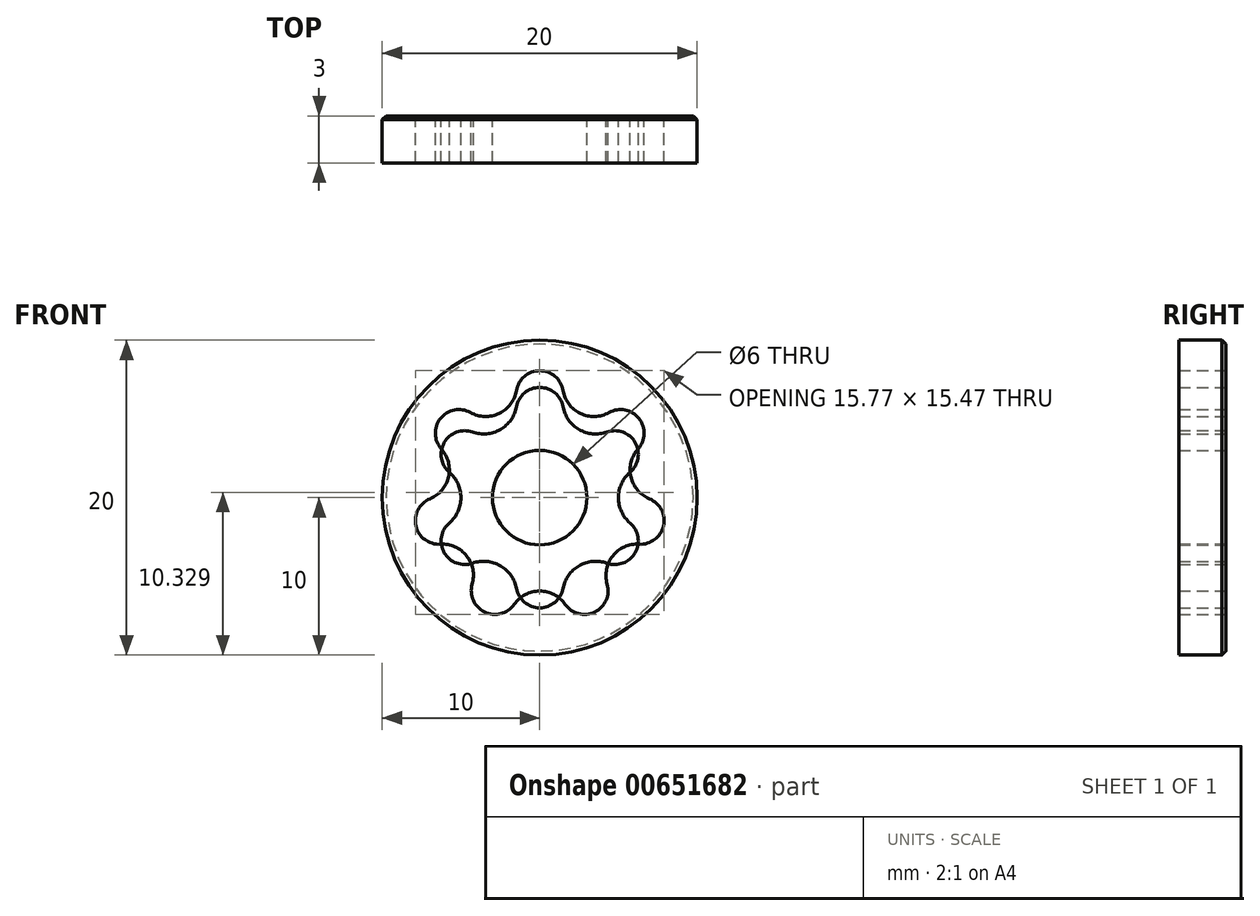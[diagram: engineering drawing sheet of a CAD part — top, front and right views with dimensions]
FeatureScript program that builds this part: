
annotation { "Feature Type Name" : "Feature", "Feature Type Description" : "" }
export const myFeature = defineFeature(function(context is Context, id is Id, definition is map)
    precondition{}
    {
        {
            var Q0;
            Q0=qCreatedBy(makeId("Front.planeOp"),FACE);
            var sketch = newSketch(context, id + "F0", { "sketchPlane" : qUnion([Q0])});
            skArc(sketch, "E0", {"start": v(1.47, 5.78) * mm, "mid": v(0, 7) * mm, "end": v(-1.47, 5.78) * mm});
            skArc(sketch, "E1", {"start": v(1.47, 5.78) * mm, "mid": v(2.5, 4.33) * mm, "end": v(4.27, 4.17) * mm});
            skArc(sketch, "E2.1.0", {"start": v(-4.27, 4.17) * mm, "mid": v(-6.06, 3.5) * mm, "end": v(-5.74, 1.61) * mm});
            skArc(sketch, "E2.1.1", {"start": v(-4.27, 4.17) * mm, "mid": v(-2.5, 4.33) * mm, "end": v(-1.47, 5.78) * mm});
            skArc(sketch, "E2.2.0", {"start": v(-5.74, -1.61) * mm, "mid": v(-6.06, -3.5) * mm, "end": v(-4.27, -4.17) * mm});
            skArc(sketch, "E2.2.1", {"start": v(-5.74, -1.61) * mm, "mid": v(-5, 0) * mm, "end": v(-5.74, 1.61) * mm});
            skArc(sketch, "E2.3.0", {"start": v(-1.47, -5.78) * mm, "mid": v(0, -7) * mm, "end": v(1.47, -5.78) * mm});
            skArc(sketch, "E2.3.1", {"start": v(-1.47, -5.78) * mm, "mid": v(-2.5, -4.33) * mm, "end": v(-4.27, -4.17) * mm});
            skArc(sketch, "E2.4.0", {"start": v(4.27, -4.17) * mm, "mid": v(6.06, -3.5) * mm, "end": v(5.74, -1.61) * mm});
            skArc(sketch, "E2.4.1", {"start": v(4.27, -4.17) * mm, "mid": v(2.5, -4.33) * mm, "end": v(1.47, -5.78) * mm});
            skArc(sketch, "E2.5.0", {"start": v(5.74, 1.61) * mm, "mid": v(6.06, 3.5) * mm, "end": v(4.27, 4.17) * mm});
            skArc(sketch, "E2.5.1", {"start": v(5.74, 1.61) * mm, "mid": v(5, 0) * mm, "end": v(5.74, -1.61) * mm});
            skPoint(sketch, "E2.center", {"position": v(0, 0) * mm});
            skLineSegment(sketch, "E3", {"start": v(0, 7) * mm, "end": v(0, -7) * mm, "construction": true});
            skLineSegment(sketch, "E4", {"start": v(0, 0) * mm, "end": v(2.5, 4.33) * mm, "construction": true});
            skCircle(sketch, "E5", {"center": v(0, 0) * mm, "radius": 3 * mm});
            skSolve(sketch);
        }
        {
            var Q0;
            Q0=makeQuery(id+"F0.imprint","IMPRINT",FACE,{"disambiguationData":[TD([[makeQuery(id+"F0.imprint","IMPRINT",EDGE,{"derivedFrom":sQuery(id+"F0.wireOp",EDGE,"E0")}),1.0]])]});
            extrude(context, id + "F1", {"entities" : qUnion([Q0]), "depth" : 3 * mm, "offsetDistance" : 25 * mm});
        }
        {
            var Q0;
            Q0=qCreatedBy(makeId("Front.planeOp"),FACE);
            var sketch = newSketch(context, id + "F2", { "sketchPlane" : qUnion([Q0])});
            skArc(sketch, "E6", {"start": v(1.48, 6.81) * mm, "mid": v(0, 8.06) * mm, "end": v(-1.48, 6.81) * mm});
            skArc(sketch, "E7", {"start": v(1.48, 6.81) * mm, "mid": v(2.58, 5.35) * mm, "end": v(4.4, 5.4) * mm});
            skArc(sketch, "E8.1.0", {"start": v(-4.4, 5.4) * mm, "mid": v(-6.3, 5.03) * mm, "end": v(-6.25, 3.09) * mm});
            skArc(sketch, "E8.1.1", {"start": v(-4.4, 5.4) * mm, "mid": v(-2.58, 5.35) * mm, "end": v(-1.48, 6.81) * mm});
            skArc(sketch, "E8.2.0", {"start": v(-6.97, -0.07) * mm, "mid": v(-7.86, -1.8) * mm, "end": v(-6.31, -2.96) * mm});
            skArc(sketch, "E8.2.1", {"start": v(-6.97, -0.07) * mm, "mid": v(-5.79, 1.32) * mm, "end": v(-6.25, 3.09) * mm});
            skArc(sketch, "E8.3.0", {"start": v(-4.29, -5.5) * mm, "mid": v(-3.5, -7.26) * mm, "end": v(-1.62, -6.78) * mm});
            skArc(sketch, "E8.3.1", {"start": v(-4.29, -5.5) * mm, "mid": v(-4.64, -3.7) * mm, "end": v(-6.31, -2.96) * mm});
            skArc(sketch, "E8.4.0", {"start": v(1.62, -6.78) * mm, "mid": v(3.5, -7.26) * mm, "end": v(4.29, -5.5) * mm});
            skArc(sketch, "E8.4.1", {"start": v(1.62, -6.78) * mm, "mid": v(0, -5.94) * mm, "end": v(-1.62, -6.78) * mm});
            skArc(sketch, "E8.5.0", {"start": v(6.31, -2.96) * mm, "mid": v(7.86, -1.8) * mm, "end": v(6.97, -0.07) * mm});
            skArc(sketch, "E8.5.1", {"start": v(6.31, -2.96) * mm, "mid": v(4.64, -3.7) * mm, "end": v(4.29, -5.5) * mm});
            skArc(sketch, "E8.6.0", {"start": v(6.25, 3.09) * mm, "mid": v(6.3, 5.03) * mm, "end": v(4.4, 5.4) * mm});
            skArc(sketch, "E8.6.1", {"start": v(6.25, 3.09) * mm, "mid": v(5.79, 1.32) * mm, "end": v(6.97, -0.07) * mm});
            skPoint(sketch, "E8.center", {"position": v(0, 0) * mm});
            skLineSegment(sketch, "E9", {"start": v(0, 8.06) * mm, "end": v(0, -5.94) * mm, "construction": true});
            skLineSegment(sketch, "E10", {"start": v(0, 1.06) * mm, "end": v(2.58, 5.35) * mm, "construction": true});
            skCircle(sketch, "E11", {"center": v(0, 0) * mm, "radius": 10 * mm});
            skPoint(sketch, "E12", {"position": v(0, 1.06) * mm});
            skSolve(sketch);
        }
        {
            var Q0;
            Q0=makeQuery(id+"F2.imprint","IMPRINT",FACE,{"disambiguationData":[TD([[makeQuery(id+"F2.imprint","IMPRINT",EDGE,{"derivedFrom":sQuery(id+"F2.wireOp",EDGE,"E6")}),-1.0]])]});
            extrude(context, id + "F3", {"entities" : qUnion([Q0]), "depth" : 3 * mm, "offsetDistance" : 25 * mm});
        }
        {
            var Q0;
            Q0=makeQuery(id+"F3.opExtrude","CAP_EDGE",EDGE,{"disambiguationData":[OSD([sQuery(id+"F2.wireOp",EDGE,"E11")])],"isStart":true});
            chamfer(context, id + "F4", {"entities" : qUnion([Q0]), "width" : 0.25 * mm, "tangentPropagation" : true});
        }
    });
